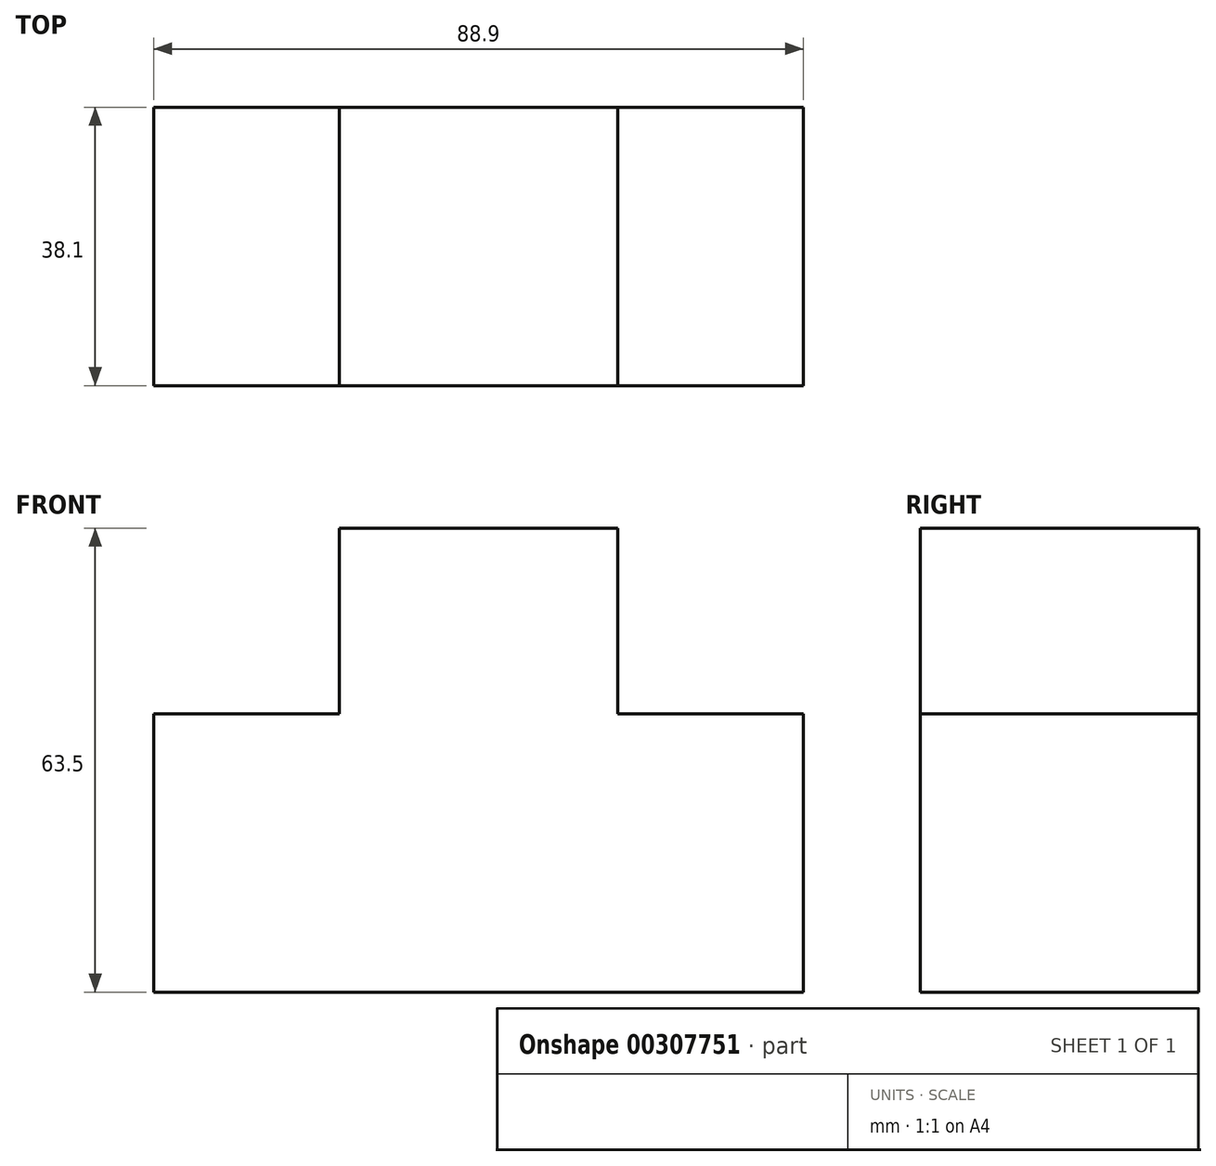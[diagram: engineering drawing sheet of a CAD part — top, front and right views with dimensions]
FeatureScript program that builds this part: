
annotation { "Feature Type Name" : "Feature", "Feature Type Description" : "" }
export const myFeature = defineFeature(function(context is Context, id is Id, definition is map)
    precondition{}
    {
        {
            var Q0;
            Q0=qCreatedBy(makeId("Front.planeOp"),FACE);
            var sketch = newSketch(context, id + "F0", { "sketchPlane" : qUnion([Q0])});
            skLineSegment(sketch, "E0", {"start": v(-43.46, -63.5) * mm, "end": v(45.44, -63.5) * mm});
            skLineSegment(sketch, "E1", {"start": v(45.44, -63.5) * mm, "end": v(45.44, -25.4) * mm});
            skLineSegment(sketch, "E2", {"start": v(45.44, -25.4) * mm, "end": v(20.04, -25.4) * mm});
            skLineSegment(sketch, "E3", {"start": v(20.04, -25.4) * mm, "end": v(20.04, 0) * mm});
            skLineSegment(sketch, "E4", {"start": v(20.04, 0) * mm, "end": v(-18.06, 0) * mm});
            skLineSegment(sketch, "E5", {"start": v(-43.46, -63.5) * mm, "end": v(-43.46, -25.4) * mm});
            skLineSegment(sketch, "E6", {"start": v(-43.46, -25.4) * mm, "end": v(-18.06, -25.4) * mm});
            skLineSegment(sketch, "E7", {"start": v(-18.06, -25.4) * mm, "end": v(-18.06, 0) * mm});
            skSolve(sketch);
        }
        {
            var Q0;
            Q0=makeQuery(id+"F0.imprint","IMPRINT",FACE,{"disambiguationData":[TD([[makeQuery(id+"F0.imprint","IMPRINT",EDGE,{"derivedFrom":sQuery(id+"F0.wireOp",EDGE,"E0")}),1.0]])]});
            extrude(context, id + "F1", {"entities" : qUnion([Q0]), "depth" : 38.1 * mm});
        }
    });
